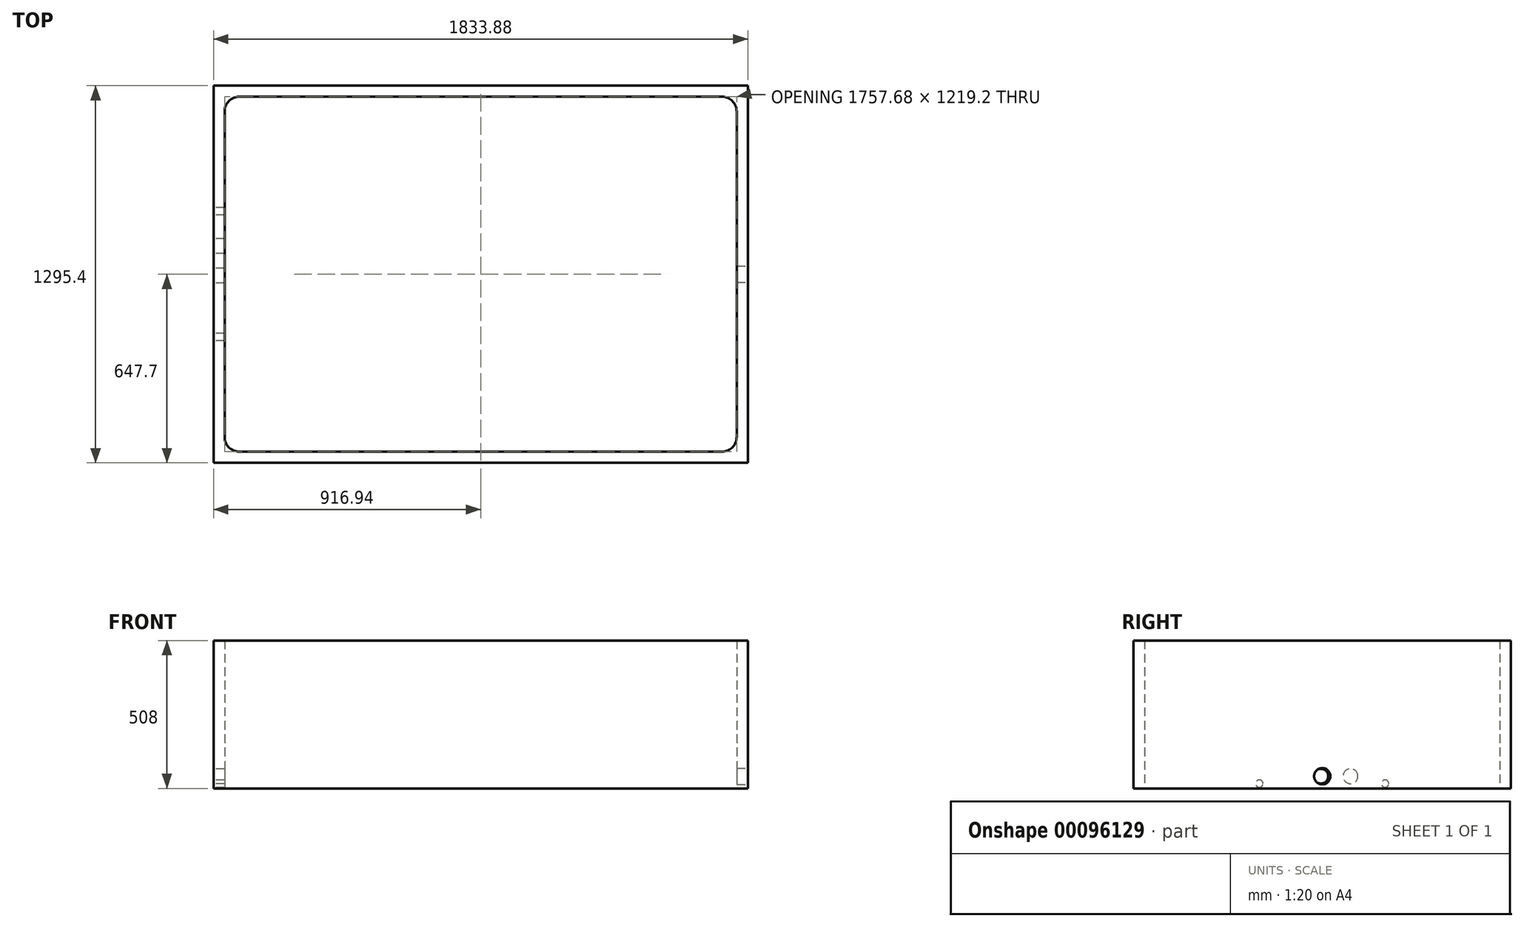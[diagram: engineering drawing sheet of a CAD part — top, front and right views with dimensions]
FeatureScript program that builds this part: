
annotation { "Feature Type Name" : "Feature", "Feature Type Description" : "" }
export const myFeature = defineFeature(function(context is Context, id is Id, definition is map)
    precondition{}
    {
        {
            var Q0;
            Q0=qCreatedBy(makeId("Top.planeOp"),FACE);
            var sketch = newSketch(context, id + "F0", { "sketchPlane" : qUnion([Q0])});
            skLineSegment(sketch, "E0.bottom", {"start": v(0, 0) * mm, "end": v(1757.68, 0) * mm});
            skLineSegment(sketch, "E0.top", {"start": v(0, 1219.2) * mm, "end": v(1757.68, 1219.2) * mm});
            skLineSegment(sketch, "E0.left", {"start": v(0, 0) * mm, "end": v(0, 1219.2) * mm});
            skLineSegment(sketch, "E0.right", {"start": v(1757.68, 0) * mm, "end": v(1757.68, 1219.2) * mm});
            skLineSegment(sketch, "E1.bottom", {"start": v(-38.1, -38.1) * mm, "end": v(1795.78, -38.1) * mm});
            skLineSegment(sketch, "E1.top", {"start": v(-38.1, 1257.3) * mm, "end": v(1795.78, 1257.3) * mm});
            skLineSegment(sketch, "E1.left", {"start": v(-38.1, -38.1) * mm, "end": v(-38.1, 1257.3) * mm});
            skLineSegment(sketch, "E1.right", {"start": v(1795.78, -38.1) * mm, "end": v(1795.78, 1257.3) * mm});
            skSolve(sketch);
        }
        {
            var Q0;
            Q0=qSketchRegion(id+"F0",true);
            extrude(context, id + "F1", {"entities" : qUnion([Q0]), "depth" : 508 * mm});
        }
        {
            var Q0;
            Q0=makeQuery(id+"F1.opExtrude","SWEPT_EDGE",EDGE,{"disambiguationData":[OSD([sQuery(id+"F0.wireOp",EDGE,"E0.top"),sQuery(id+"F0.wireOp",EDGE,"E0.right")])]});
            fillet(context, id + "F2", {"entities" : qUnion([Q0]), "radius" : 50.8 * mm, "tangentPropagation" : true, "allowEdgeOverflow" : false});
        }
        {
            var Q0;
            Q0=makeQuery(id+"F1.opExtrude","SWEPT_EDGE",EDGE,{"disambiguationData":[OSD([sQuery(id+"F0.wireOp",EDGE,"E0.top"),sQuery(id+"F0.wireOp",EDGE,"E0.left")])]});
            fillet(context, id + "F3", {"entities" : qUnion([Q0]), "radius" : 50.8 * mm, "tangentPropagation" : true, "allowEdgeOverflow" : false});
        }
        {
            var Q0;
            Q0=makeQuery(id+"F1.opExtrude","SWEPT_EDGE",EDGE,{"disambiguationData":[OSD([sQuery(id+"F0.wireOp",EDGE,"E0.bottom"),sQuery(id+"F0.wireOp",EDGE,"E0.right")])]});
            fillet(context, id + "F4", {"entities" : qUnion([Q0]), "radius" : 50.8 * mm, "tangentPropagation" : true, "allowEdgeOverflow" : false});
        }
        {
            var Q0;
            Q0=makeQuery(id+"F1.opExtrude","SWEPT_EDGE",EDGE,{"disambiguationData":[OSD([sQuery(id+"F0.wireOp",EDGE,"E0.bottom"),sQuery(id+"F0.wireOp",EDGE,"E0.left")])]});
            fillet(context, id + "F5", {"entities" : qUnion([Q0]), "radius" : 50.8 * mm, "tangentPropagation" : true, "allowEdgeOverflow" : false});
        }
        {
            var Q0;
            Q0=makeQuery(id+"F1.opExtrude","SWEPT_FACE",FACE,{"disambiguationData":[OSD([sQuery(id+"F0.wireOp",EDGE,"E1.left")])]});
            var sketch = newSketch(context, id + "F6", { "sketchPlane" : qUnion([Q0])});
            skCircle(sketch, "E2", {"center": v(-604.98, 41.91) * mm, "radius": 25.4 * mm});
            skCircle(sketch, "E3", {"center": v(-706.58, 41.91) * mm, "radius": 25.4 * mm});
            skSolve(sketch);
        }
        {
            var Q0;
            Q0=makeQuery(id+"F6.imprint","IMPRINT",FACE,{"disambiguationData":[TD([[makeQuery(id+"F6.imprint","IMPRINT",EDGE,{"derivedFrom":sQuery(id+"F6.wireOp",EDGE,"E2")}),-1.0]])]});
            var sketch = newSketch(context, id + "F7", { "sketchPlane" : qUnion([Q0])});
            skCircle(sketch, "E4", {"center": v(-393.7, 16.51) * mm, "radius": 12.7 * mm});
            skCircle(sketch, "E5", {"center": v(-825.5, 16.51) * mm, "radius": 12.7 * mm});
            skSolve(sketch);
        }
        {
            var Q0;
            Q0=qSketchRegion(id+"F6",true);
            extrude(context, id + "F8", {"entities" : qUnion([Q0]), "operationType" : NewBodyOperationType.REMOVE, "oppositeDirection" : true, "depth" : 50.8 * mm});
        }
        {
            var Q0;
            Q0=qSketchRegion(id+"F7",true);
            extrude(context, id + "F9", {"entities" : qUnion([Q0]), "operationType" : NewBodyOperationType.REMOVE, "oppositeDirection" : true, "depth" : 50.8 * mm});
        }
        {
            var Q0;
            Q0=makeQuery(id+"F1.opExtrude","SWEPT_FACE",FACE,{"disambiguationData":[OSD([sQuery(id+"F0.wireOp",EDGE,"E1.right")])]});
            var sketch = newSketch(context, id + "F10", { "sketchPlane" : qUnion([Q0])});
            skCircle(sketch, "E6", {"center": v(609.6, 41.91) * mm, "radius": 27.86 * mm});
            skSolve(sketch);
        }
        {
            var Q0;
            Q0=qSketchRegion(id+"F10",true);
            extrude(context, id + "F11", {"entities" : qUnion([Q0]), "operationType" : NewBodyOperationType.REMOVE, "oppositeDirection" : true, "depth" : 50.8 * mm});
        }
    });
